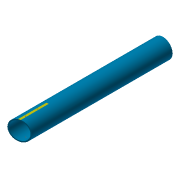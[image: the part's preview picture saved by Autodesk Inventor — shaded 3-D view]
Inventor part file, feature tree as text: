
AUTODESK INVENTOR PART (.ipt)
format: ipt  version: 2016 (Build 200138000, 138)  size: 134,656 bytes
history: native  units: in
note: dims shown in document units (in); Inventor stores cm internally (conversion verified against a paired STEP export)
features: sketch x7, extrude x4, plane x3, hole x1, other x1
ambient origin geometry x8: Origin, YZ Plane, XZ Plane, XY Plane, X Axis, Y Axis, Z Axis, Center Point
bodies: Solid1 (feature_tree)
feature tree (16):
  extrude  "Extrusion1"  Depth=0.1417in
  sketch  "Sketch18"  dims[d3=18.7402in d4=0.0in d60=15.0deg]
  plane  "Work Plane9"
  extrude  "Extrusion11"  TaperAngle=15.0deg  [1 undecoded]
  sketch  "Sketch20"  dims[d64=0.3937in d65=3.937in]
  plane  "Work Plane10"
  plane  "Work Plane11"
  extrude  "flat1"  Depth=1.0in TaperAngle=0.0deg
  extrude  "flat2"  Depth=0.3937in
  hole  "Hole1"  [1 undecoded]
  sketch  "Sketch1"  dims[d0=2.4803in d2=0.1417in]
  other  "Work Axis2"
  sketch  "Sketch19"  dims[d61=4.0in d62=1.0in d63=0.0in]
  sketch  "Sketch21"  dims[d66=0.01in d67=0.0in d68=0.3937in]
  sketch  "Sketch22"  dims[d69=3.937in]
  sketch  "Sketch23"  dims[d70=0.01in d71=0.0in d73=1.5748in d74=0.7874in d75=0.125in d76=0.75in d77=0.375in d78=0.25in d79=0.5635in d80=1.0in d81=0.8108in d82=14.8031in d83=14.8031in]
note: 2 required parameter values undecoded (feature->parameter linkage not recoverable at this tier; creation-order binding heuristic only, values carry confidence <= 0.55)
